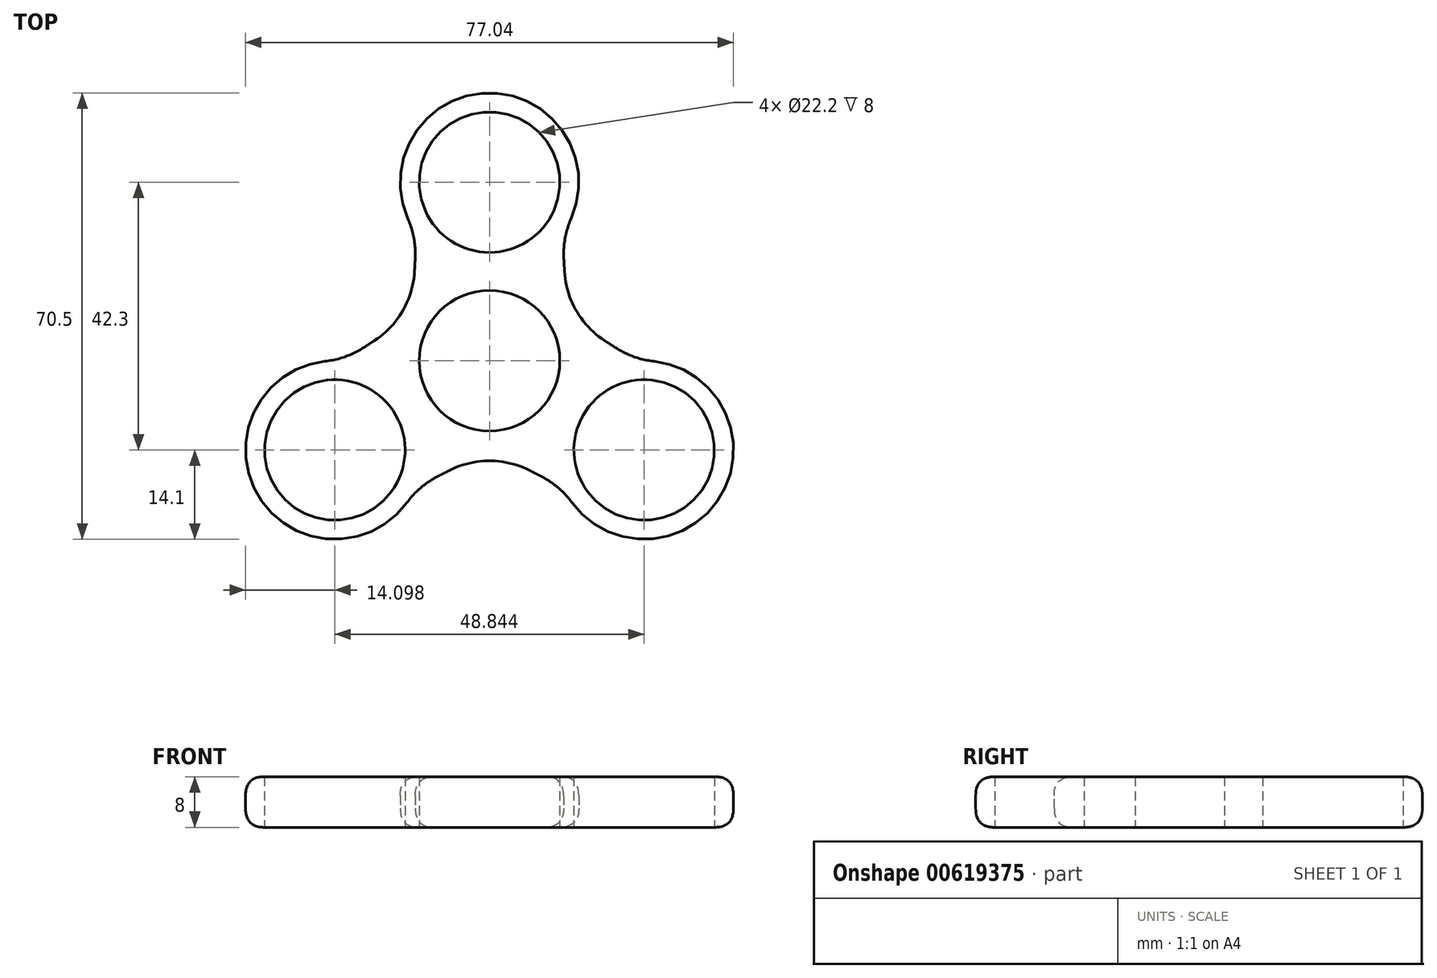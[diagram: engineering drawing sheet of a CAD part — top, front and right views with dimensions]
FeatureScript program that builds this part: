
annotation { "Feature Type Name" : "Feature", "Feature Type Description" : "" }
export const myFeature = defineFeature(function(context is Context, id is Id, definition is map)
    precondition{}
    {
        {
            var Q0;
            Q0=qCreatedBy(makeId("Top.planeOp"),FACE);
            var sketch = newSketch(context, id + "F0", { "sketchPlane" : qUnion([Q0])});
            skCircle(sketch, "E0", {"center": v(0, 0) * mm, "radius": 14.1 * mm});
            skLineSegment(sketch, "E1", {"start": v(0, 0) * mm, "end": v(0, 28.2) * mm});
            skLineSegment(sketch, "E2", {"start": v(0, 0) * mm, "end": v(24.42, -14.1) * mm});
            skLineSegment(sketch, "E3", {"start": v(24.42, -14.1) * mm, "end": v(0, 0) * mm});
            skLineSegment(sketch, "E4", {"start": v(0, 0) * mm, "end": v(-24.42, -14.1) * mm});
            skCircle(sketch, "E5", {"center": v(24.42, -14.1) * mm, "radius": 14.1 * mm});
            skCircle(sketch, "E6", {"center": v(0, 28.2) * mm, "radius": 14.1 * mm});
            skCircle(sketch, "E7", {"center": v(-24.42, -14.1) * mm, "radius": 14.1 * mm});
            skCircle(sketch, "E8.0", {"center": v(0, 28.2) * mm, "radius": 11.1 * mm});
            skCircle(sketch, "E9.0", {"center": v(-24.42, -14.1) * mm, "radius": 11.1 * mm});
            skCircle(sketch, "E10.0", {"center": v(24.42, -14.1) * mm, "radius": 11.1 * mm});
            skLineSegment(sketch, "E11", {"start": v(11.1, 28.2) * mm, "end": v(0, 28.2) * mm});
            skLineSegment(sketch, "E12", {"start": v(11.1, 28.2) * mm, "end": v(11.1, 28.2) * mm});
            skLineSegment(sketch, "E13", {"start": v(-24.42, -14.1) * mm, "end": v(-29.97, -4.49) * mm});
            skLineSegment(sketch, "E14", {"start": v(-29.97, -4.49) * mm, "end": v(-24.42, -14.1) * mm});
            skLineSegment(sketch, "E15", {"start": v(-24.42, -14.1) * mm, "end": v(-18.87, -23.71) * mm});
            skLineSegment(sketch, "E16", {"start": v(24.42, -14.1) * mm, "end": v(18.87, -23.71) * mm});
            skLineSegment(sketch, "E17", {"start": v(18.87, -23.71) * mm, "end": v(24.42, -14.1) * mm});
            skLineSegment(sketch, "E18", {"start": v(24.42, -14.1) * mm, "end": v(29.97, -4.49) * mm});
            skLineSegment(sketch, "E19", {"start": v(0, 0) * mm, "end": v(0, -14.1) * mm});
            skLineSegment(sketch, "E20", {"start": v(0, -14.1) * mm, "end": v(0, 0) * mm});
            skLineSegment(sketch, "E21", {"start": v(18.87, -23.71) * mm, "end": v(0, -14.1) * mm});
            skLineSegment(sketch, "E22", {"start": v(0, -14.1) * mm, "end": v(-18.87, -23.71) * mm});
            skCircle(sketch, "E23.0", {"center": v(0, 0) * mm, "radius": 11.1 * mm});
            skLineSegment(sketch, "E24", {"start": v(0, 28.2) * mm, "end": v(-11.1, 28.2) * mm});
            skLineSegment(sketch, "E25", {"start": v(0, 0) * mm, "end": v(-9.61, 5.55) * mm});
            skLineSegment(sketch, "E26", {"start": v(-9.61, 5.55) * mm, "end": v(0, 0) * mm});
            skLineSegment(sketch, "E27", {"start": v(9.61, 5.55) * mm, "end": v(0, 0) * mm});
            skLineSegment(sketch, "E28", {"start": v(-9.61, 5.55) * mm, "end": v(-26.22, 15.14) * mm});
            skLineSegment(sketch, "E29", {"start": v(9.61, 5.55) * mm, "end": v(26.22, 15.14) * mm});
            skLineSegment(sketch, "E30", {"start": v(-29.97, -4.49) * mm, "end": v(-12.21, 7.05) * mm});
            skLineSegment(sketch, "E31", {"start": v(-12.21, 7.05) * mm, "end": v(-11.1, 28.2) * mm});
            skLineSegment(sketch, "E32", {"start": v(11.1, 28.2) * mm, "end": v(12.21, 7.05) * mm});
            skLineSegment(sketch, "E33", {"start": v(12.21, 7.05) * mm, "end": v(29.97, -4.49) * mm});
            skSolve(sketch);
        }
        {
            var Q0;
            Q0 = qSketchRegion(id + "F0", true);
            extrude(context, id + "F1", {"entities" : qUnion([Q0]), "depth" : 8 * mm, "offsetDistance" : 25 * mm});
        }
        {
            var Q0;
            Q0=makeQuery(id+"F1.opExtrude","SWEPT_EDGE",EDGE,{"disambiguationData":[OSD([sQuery(id+"F0.wireOp",EDGE,"E0"),sQuery(id+"F0.wireOp",EDGE,"75cguXxj-y3vR-SGKv-tKED-M2nO4OH2yCkN"),sQuery(id+"F0.wireOp",EDGE,"lJh22VZ6-SqfV-RVuy-xCzw-MPuz3jTHnhMM")])]});
            var Q1;
            Q1=makeQuery(id+"F1.opExtrude","SWEPT_EDGE",EDGE,{"disambiguationData":[OSD([sQuery(id+"F0.wireOp",EDGE,"E6"),sQuery(id+"F0.wireOp",EDGE,"lJh22VZ6-SqfV-RVuy-xCzw-MPuz3jTHnhMM")])]});
            var Q2;
            Q2=makeQuery(id+"F1.opExtrude","SWEPT_EDGE",EDGE,{"disambiguationData":[OSD([sQuery(id+"F0.wireOp",EDGE,"E6"),sQuery(id+"F0.wireOp",EDGE,"lKjXrUZr-bwT0-XL3y-ZAQc-yOHY5e1dj1Xq")])]});
            var Q3;
            Q3=makeQuery(id+"F1.opExtrude","SWEPT_EDGE",EDGE,{"disambiguationData":[OSD([sQuery(id+"F0.wireOp",EDGE,"E0"),sQuery(id+"F0.wireOp",EDGE,"UHfG0yOH-JprN-kARH-kS1Q-DhYVzWg3x8zM"),sQuery(id+"F0.wireOp",EDGE,"lKjXrUZr-bwT0-XL3y-ZAQc-yOHY5e1dj1Xq")])]});
            var Q4;
            Q4=makeQuery(id+"F1.opExtrude","SWEPT_EDGE",EDGE,{"disambiguationData":[OSD([sQuery(id+"F0.wireOp",EDGE,"E7"),sQuery(id+"F0.wireOp",EDGE,"UHfG0yOH-JprN-kARH-kS1Q-DhYVzWg3x8zM")])]});
            var Q5;
            Q5=makeQuery(id+"F1.opExtrude","SWEPT_EDGE",EDGE,{"disambiguationData":[OSD([sQuery(id+"F0.wireOp",EDGE,"E7"),sQuery(id+"F0.wireOp",EDGE,"E22")])]});
            var Q6;
            Q6=makeQuery(id+"F1.opExtrude","SWEPT_EDGE",EDGE,{"disambiguationData":[OSD([sQuery(id+"F0.wireOp",EDGE,"E0"),sQuery(id+"F0.wireOp",EDGE,"E20"),sQuery(id+"F0.wireOp",EDGE,"E21"),sQuery(id+"F0.wireOp",EDGE,"E22")])]});
            var Q7;
            Q7=makeQuery(id+"F1.opExtrude","SWEPT_EDGE",EDGE,{"disambiguationData":[OSD([sQuery(id+"F0.wireOp",EDGE,"E5"),sQuery(id+"F0.wireOp",EDGE,"E21")])]});
            var Q8;
            Q8=makeQuery(id+"F1.opExtrude","SWEPT_EDGE",EDGE,{"disambiguationData":[OSD([sQuery(id+"F0.wireOp",EDGE,"E5"),sQuery(id+"F0.wireOp",EDGE,"75cguXxj-y3vR-SGKv-tKED-M2nO4OH2yCkN")])]});
            fillet(context, id + "F2", {"entities" : qUnion([Q0, Q1, Q2, Q3, Q4, Q5, Q6, Q7, Q8]), "radius" : 14 * mm, "tangentPropagation" : true, "allowEdgeOverflow" : false});
        }
        {
            var Q0;
            Q0=makeQuery(id+"F1.opExtrude","CAP_EDGE",EDGE,{"disambiguationData":[OSD([sQuery(id+"F0.wireOp",EDGE,"E6")])],"isStart":false});
            var Q1;
            {var subQ0=sQuery(id+"F0.wireOp",EDGE,"lKjXrUZr-bwT0-XL3y-ZAQc-yOHY5e1dj1Xq");var subQ1=sQuery(id+"F0.wireOp",EDGE,"E6");Q1=makeQuery(id+"F2.opFillet","BLEND_EDGE",EDGE,{"blendedFrom":[makeQuery(id+"F1.opExtrude","SWEPT_EDGE",EDGE,{"disambiguationData":[OSD([subQ1,subQ0])]}),makeQuery(id+"F1.opExtrude","CAP_FACE",FACE,{"disambiguationData":[OSD([sQuery(id+"F0.wireOp",EDGE,"E5"),subQ1,sQuery(id+"F0.wireOp",EDGE,"E7"),sQuery(id+"F0.wireOp",EDGE,"E8.0"),sQuery(id+"F0.wireOp",EDGE,"E9.0"),sQuery(id+"F0.wireOp",EDGE,"E10.0"),sQuery(id+"F0.wireOp",EDGE,"UHfG0yOH-JprN-kARH-kS1Q-DhYVzWg3x8zM"),subQ0,sQuery(id+"F0.wireOp",EDGE,"E21"),sQuery(id+"F0.wireOp",EDGE,"E22"),sQuery(id+"F0.wireOp",EDGE,"E23.0"),sQuery(id+"F0.wireOp",EDGE,"75cguXxj-y3vR-SGKv-tKED-M2nO4OH2yCkN"),sQuery(id+"F0.wireOp",EDGE,"lJh22VZ6-SqfV-RVuy-xCzw-MPuz3jTHnhMM")])],"isStart":false})],"blendedInto":[makeQuery(id+"F1.opExtrude","CAP_FACE",FACE,{"disambiguationData":[OSD([sQuery(id+"F0.wireOp",EDGE,"E5"),subQ1,sQuery(id+"F0.wireOp",EDGE,"E7"),sQuery(id+"F0.wireOp",EDGE,"E8.0"),sQuery(id+"F0.wireOp",EDGE,"E9.0"),sQuery(id+"F0.wireOp",EDGE,"E10.0"),sQuery(id+"F0.wireOp",EDGE,"UHfG0yOH-JprN-kARH-kS1Q-DhYVzWg3x8zM"),subQ0,sQuery(id+"F0.wireOp",EDGE,"E21"),sQuery(id+"F0.wireOp",EDGE,"E22"),sQuery(id+"F0.wireOp",EDGE,"E23.0"),sQuery(id+"F0.wireOp",EDGE,"75cguXxj-y3vR-SGKv-tKED-M2nO4OH2yCkN"),sQuery(id+"F0.wireOp",EDGE,"lJh22VZ6-SqfV-RVuy-xCzw-MPuz3jTHnhMM")])],"isStart":false})]});}
            var Q2;
            {var subQ0=sQuery(id+"F0.wireOp",EDGE,"lKjXrUZr-bwT0-XL3y-ZAQc-yOHY5e1dj1Xq");var subQ1=sQuery(id+"F0.wireOp",EDGE,"UHfG0yOH-JprN-kARH-kS1Q-DhYVzWg3x8zM");Q2=makeQuery(id+"F2.opFillet","BLEND_EDGE",EDGE,{"blendedFrom":[makeQuery(id+"F1.opExtrude","SWEPT_EDGE",EDGE,{"disambiguationData":[OSD([sQuery(id+"F0.wireOp",EDGE,"E0"),subQ1,subQ0])]}),makeQuery(id+"F1.opExtrude","CAP_FACE",FACE,{"disambiguationData":[OSD([sQuery(id+"F0.wireOp",EDGE,"E5"),sQuery(id+"F0.wireOp",EDGE,"E6"),sQuery(id+"F0.wireOp",EDGE,"E7"),sQuery(id+"F0.wireOp",EDGE,"E8.0"),sQuery(id+"F0.wireOp",EDGE,"E9.0"),sQuery(id+"F0.wireOp",EDGE,"E10.0"),subQ1,subQ0,sQuery(id+"F0.wireOp",EDGE,"E21"),sQuery(id+"F0.wireOp",EDGE,"E22"),sQuery(id+"F0.wireOp",EDGE,"E23.0"),sQuery(id+"F0.wireOp",EDGE,"75cguXxj-y3vR-SGKv-tKED-M2nO4OH2yCkN"),sQuery(id+"F0.wireOp",EDGE,"lJh22VZ6-SqfV-RVuy-xCzw-MPuz3jTHnhMM")])],"isStart":false})],"blendedInto":[makeQuery(id+"F1.opExtrude","CAP_FACE",FACE,{"disambiguationData":[OSD([sQuery(id+"F0.wireOp",EDGE,"E5"),sQuery(id+"F0.wireOp",EDGE,"E6"),sQuery(id+"F0.wireOp",EDGE,"E7"),sQuery(id+"F0.wireOp",EDGE,"E8.0"),sQuery(id+"F0.wireOp",EDGE,"E9.0"),sQuery(id+"F0.wireOp",EDGE,"E10.0"),subQ1,subQ0,sQuery(id+"F0.wireOp",EDGE,"E21"),sQuery(id+"F0.wireOp",EDGE,"E22"),sQuery(id+"F0.wireOp",EDGE,"E23.0"),sQuery(id+"F0.wireOp",EDGE,"75cguXxj-y3vR-SGKv-tKED-M2nO4OH2yCkN"),sQuery(id+"F0.wireOp",EDGE,"lJh22VZ6-SqfV-RVuy-xCzw-MPuz3jTHnhMM")])],"isStart":false})]});}
            var Q3;
            {var subQ0=sQuery(id+"F0.wireOp",EDGE,"UHfG0yOH-JprN-kARH-kS1Q-DhYVzWg3x8zM");var subQ1=sQuery(id+"F0.wireOp",EDGE,"E7");Q3=makeQuery(id+"F2.opFillet","BLEND_EDGE",EDGE,{"blendedFrom":[makeQuery(id+"F1.opExtrude","SWEPT_EDGE",EDGE,{"disambiguationData":[OSD([subQ1,subQ0])]}),makeQuery(id+"F1.opExtrude","CAP_FACE",FACE,{"disambiguationData":[OSD([sQuery(id+"F0.wireOp",EDGE,"E5"),sQuery(id+"F0.wireOp",EDGE,"E6"),subQ1,sQuery(id+"F0.wireOp",EDGE,"E8.0"),sQuery(id+"F0.wireOp",EDGE,"E9.0"),sQuery(id+"F0.wireOp",EDGE,"E10.0"),subQ0,sQuery(id+"F0.wireOp",EDGE,"lKjXrUZr-bwT0-XL3y-ZAQc-yOHY5e1dj1Xq"),sQuery(id+"F0.wireOp",EDGE,"E21"),sQuery(id+"F0.wireOp",EDGE,"E22"),sQuery(id+"F0.wireOp",EDGE,"E23.0"),sQuery(id+"F0.wireOp",EDGE,"75cguXxj-y3vR-SGKv-tKED-M2nO4OH2yCkN"),sQuery(id+"F0.wireOp",EDGE,"lJh22VZ6-SqfV-RVuy-xCzw-MPuz3jTHnhMM")])],"isStart":false})],"blendedInto":[makeQuery(id+"F1.opExtrude","CAP_FACE",FACE,{"disambiguationData":[OSD([sQuery(id+"F0.wireOp",EDGE,"E5"),sQuery(id+"F0.wireOp",EDGE,"E6"),subQ1,sQuery(id+"F0.wireOp",EDGE,"E8.0"),sQuery(id+"F0.wireOp",EDGE,"E9.0"),sQuery(id+"F0.wireOp",EDGE,"E10.0"),subQ0,sQuery(id+"F0.wireOp",EDGE,"lKjXrUZr-bwT0-XL3y-ZAQc-yOHY5e1dj1Xq"),sQuery(id+"F0.wireOp",EDGE,"E21"),sQuery(id+"F0.wireOp",EDGE,"E22"),sQuery(id+"F0.wireOp",EDGE,"E23.0"),sQuery(id+"F0.wireOp",EDGE,"75cguXxj-y3vR-SGKv-tKED-M2nO4OH2yCkN"),sQuery(id+"F0.wireOp",EDGE,"lJh22VZ6-SqfV-RVuy-xCzw-MPuz3jTHnhMM")])],"isStart":false})]});}
            var Q4;
            Q4=makeQuery(id+"F1.opExtrude","CAP_EDGE",EDGE,{"disambiguationData":[OSD([sQuery(id+"F0.wireOp",EDGE,"E7")])],"isStart":true});
            var Q5;
            Q5=makeQuery(id+"F1.opExtrude","CAP_EDGE",EDGE,{"disambiguationData":[OSD([sQuery(id+"F0.wireOp",EDGE,"E6")])],"isStart":true});
            fillet(context, id + "F3", {"entities" : qUnion([Q0, Q1, Q2, Q3, Q4, Q5]), "radius" : 3 * mm, "tangentPropagation" : true, "rho" : .5, "crossSection" : FilletCrossSection.CONIC, "allowEdgeOverflow" : false});
        }
    });
